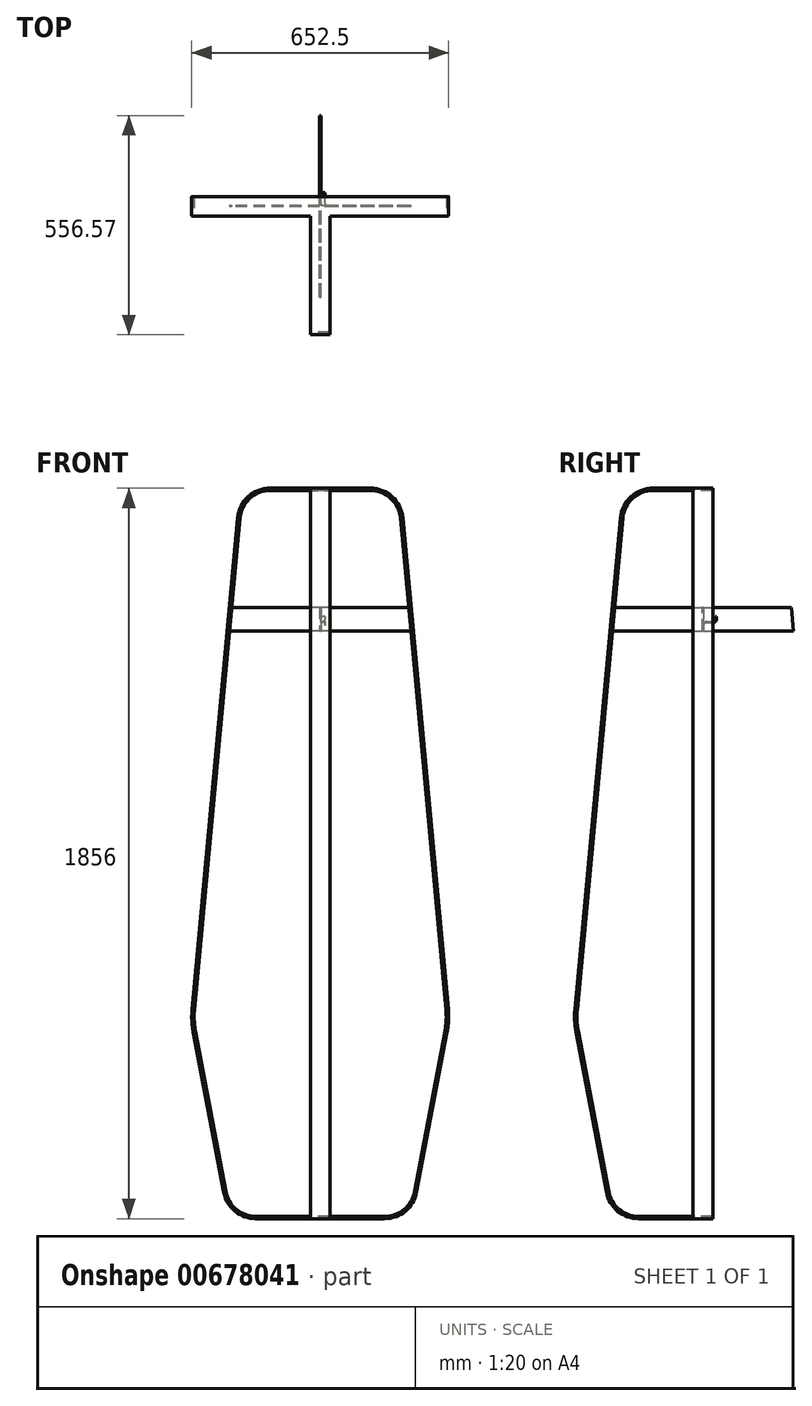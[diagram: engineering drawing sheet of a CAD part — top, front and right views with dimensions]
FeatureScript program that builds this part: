
annotation { "Feature Type Name" : "Feature", "Feature Type Description" : "" }
export const myFeature = defineFeature(function(context is Context, id is Id, definition is map)
    precondition{}
    {
        {
            var Q0;
            Q0=qCreatedBy(makeId("Front.planeOp"),FACE);
            var sketch = newSketch(context, id + "F0", { "sketchPlane" : qUnion([Q0])});
            skLineSegment(sketch, "E0", {"start": v(0, 0) * mm, "end": v(163.77, 0) * mm, "construction": true});
            skLineSegment(sketch, "E1", {"start": v(242.36, 65.07) * mm, "end": v(325, 500) * mm, "construction": true});
            skLineSegment(sketch, "E2", {"start": v(325, 500) * mm, "end": v(206.72, 1777.38) * mm, "construction": true});
            skLineSegment(sketch, "E3", {"start": v(127.07, 1850) * mm, "end": v(0, 1850) * mm, "construction": true});
            skLineSegment(sketch, "E4", {"start": v(0, 1850) * mm, "end": v(0, 0) * mm, "construction": true});
            skLineSegment(sketch, "E5", {"start": v(325, 500) * mm, "end": v(0, 500) * mm, "construction": true});
            skPoint(sketch, "E6.visualSharp", {"position": v(200, 1850) * mm});
            skArc(sketch, "E6.filletArc", {"start": v(206.72, 1777.38) * mm, "mid": v(180.96, 1829.12) * mm, "end": v(127.07, 1850) * mm, "construction": true});
            skPoint(sketch, "E7.visualSharp", {"position": v(230, 0) * mm});
            skArc(sketch, "E7.filletArc", {"start": v(163.77, 0) * mm, "mid": v(214.79, 18.38) * mm, "end": v(242.36, 65.07) * mm, "construction": true});
            skArc(sketch, "E8", {"start": v(319.74, 472.3) * mm, "mid": v(323.02, 500.1) * mm, "end": v(322.4, 528.07) * mm, "construction": true});
            skLineSegment(sketch, "E9", {"start": v(227.78, 1550) * mm, "end": v(0, 1550) * mm, "construction": true});
            skSolve(sketch);
        }
        {
            var Q0;
            Q0=qCreatedBy(makeId("Front.planeOp"),FACE);
            var sketch = newSketch(context, id + "F1", { "sketchPlane" : qUnion([Q0])});
            skLineSegment(sketch, "E10", {"start": v(0, 0) * mm, "end": v(163.77, 0) * mm});
            skArc(sketch, "E11", {"start": v(163.77, 0) * mm, "mid": v(214.79, 18.38) * mm, "end": v(242.36, 65.07) * mm});
            skLineSegment(sketch, "E12", {"start": v(322.4, 528.07) * mm, "end": v(206.72, 1777.38) * mm});
            skArc(sketch, "E13", {"start": v(206.72, 1777.38) * mm, "mid": v(180.96, 1829.12) * mm, "end": v(127.07, 1850) * mm});
            skLineSegment(sketch, "E14", {"start": v(127.07, 1850) * mm, "end": v(0, 1850) * mm});
            skLineSegment(sketch, "E15", {"start": v(242.36, 65.07) * mm, "end": v(319.74, 472.3) * mm});
            skArc(sketch, "E16", {"start": v(319.74, 472.3) * mm, "mid": v(323.02, 500.1) * mm, "end": v(322.4, 528.07) * mm});
            skSolve(sketch);
        }
        {
            var Q0;
            Q0=qCreatedBy(makeId("Right.planeOp"),FACE);
            var sketch = newSketch(context, id + "F2", { "sketchPlane" : qUnion([Q0])});
            skLineSegment(sketch, "E17.bottom", {"start": v(25, 3) * mm, "end": v(-25, 3) * mm});
            skLineSegment(sketch, "E17.top", {"start": v(25, -3) * mm, "end": v(-25, -3) * mm});
            skLineSegment(sketch, "E17.left", {"start": v(25, 3) * mm, "end": v(25, -3) * mm});
            skLineSegment(sketch, "E17.right", {"start": v(-25, 3) * mm, "end": v(-25, -3) * mm});
            skPoint(sketch, "E17.middle", {"position": v(0, 0) * mm});
            skSolve(sketch);
        }
        {
            var Q0;
            Q0 = qSketchRegion(id + "F2", true);
            var Q1;
            Q1=sQuery(id+"F1.wireOp",EDGE,"E10");
            var Q2;
            Q2=sQuery(id+"F1.wireOp",EDGE,"E11");
            var Q3;
            Q3=sQuery(id+"F1.wireOp",EDGE,"E15");
            var Q4;
            Q4=sQuery(id+"F1.wireOp",EDGE,"E16");
            var Q5;
            Q5=sQuery(id+"F1.wireOp",EDGE,"E12");
            var Q6;
            Q6=sQuery(id+"F1.wireOp",EDGE,"E13");
            var Q7;
            Q7=sQuery(id+"F1.wireOp",EDGE,"E14");
            sweep(context, id + "F3", {"profiles" : qUnion([Q0]), "path" : qUnion([Q1, Q2, Q3, Q4, Q5, Q6, Q7])});
        }
        {
            var Q0;
            Q0=qCreatedBy(makeId("Right.planeOp"),FACE);
            var sketch = newSketch(context, id + "F4", { "sketchPlane" : qUnion([Q0])});
            skLineSegment(sketch, "E18.bottom", {"start": v(1.5, 1550) * mm, "end": v(-1.5, 1550) * mm});
            skLineSegment(sketch, "E18.top", {"start": v(1.5, 1490) * mm, "end": v(-1.5, 1490) * mm});
            skLineSegment(sketch, "E18.left", {"start": v(1.5, 1550) * mm, "end": v(1.5, 1490) * mm});
            skLineSegment(sketch, "E18.right", {"start": v(-1.5, 1550) * mm, "end": v(-1.5, 1490) * mm});
            skPoint(sketch, "E18.middle", {"position": v(0, 1520) * mm});
            skSolve(sketch);
        }
        {
            var Q0;
            Q0=qCreatedBy(makeId("Right.planeOp"),FACE);
            var sketch = newSketch(context, id + "F5", { "sketchPlane" : qUnion([Q0])});
            skLineSegment(sketch, "E19.bottom", {"start": v(1.5, 1504) * mm, "end": v(-1.5, 1504) * mm, "construction": true});
            skLineSegment(sketch, "E19.top", {"start": v(1.5, 1490) * mm, "end": v(-1.5, 1490) * mm});
            skLineSegment(sketch, "E19.left", {"start": v(1.5, 1504) * mm, "end": v(1.5, 1490) * mm});
            skLineSegment(sketch, "E19.right", {"start": v(-1.5, 1504) * mm, "end": v(-1.5, 1490) * mm});
            skPoint(sketch, "E19.middle", {"position": v(0, 1497) * mm});
            skArc(sketch, "E20", {"start": v(8.5, 1514) * mm, "mid": v(1.43, 1511.07) * mm, "end": v(-1.5, 1504) * mm});
            skArc(sketch, "E21", {"start": v(8.5, 1511) * mm, "mid": v(3.55, 1508.95) * mm, "end": v(1.5, 1504) * mm});
            skLineSegment(sketch, "E22", {"start": v(8.5, 1511) * mm, "end": v(24.5, 1511) * mm});
            skLineSegment(sketch, "E23", {"start": v(8.5, 1514) * mm, "end": v(24.5, 1514) * mm});
            skArc(sketch, "E24", {"start": v(24.5, 1514) * mm, "mid": v(29.45, 1516.05) * mm, "end": v(31.5, 1521) * mm});
            skArc(sketch, "E25", {"start": v(24.5, 1511) * mm, "mid": v(31.57, 1513.93) * mm, "end": v(34.5, 1521) * mm});
            skLineSegment(sketch, "E26", {"start": v(31.5, 1521) * mm, "end": v(31.5, 1527) * mm});
            skLineSegment(sketch, "E27", {"start": v(31.5, 1527) * mm, "end": v(34.5, 1527) * mm});
            skLineSegment(sketch, "E28", {"start": v(34.5, 1527) * mm, "end": v(34.5, 1521) * mm});
            skSolve(sketch);
        }
        {
            var Q0;
            Q0 = qSketchRegion(id + "F5", true);
            extrude(context, id + "F6", {"entities" : qUnion([Q0]), "depth" : 12 * mm, "offsetDistance" : 25 * mm});
        }
        {
            var Q0;
            Q0=makeQuery(id+"F3.opSweep","SWEPT_BODY",BODY,{"disambiguationData":[OSD([sQuery(id+"F1.wireOp",EDGE,"E14"),sQuery(id+"F2.wireOp",EDGE,"E17.bottom"),sQuery(id+"F2.wireOp",EDGE,"E17.top"),sQuery(id+"F2.wireOp",EDGE,"E17.left"),sQuery(id+"F2.wireOp",EDGE,"E17.right")])]});
            var Q1;
            Q1=qCreatedBy(makeId("Right.planeOp"),FACE);
            mirror(context, id + "F7", {"operationType" : NewBodyOperationType.ADD, "entities" : qUnion([Q0]), "mirrorPlane" : qUnion([Q1])});
        }
        {
            var Q0;
            Q0 = qSketchRegion(id + "F4", true);
            extrude(context, id + "F8", {"entities" : qUnion([Q0]), "endBound" : BoundingType.UP_TO_NEXT, "depth" : 25 * mm, "offsetDistance" : 25 * mm, "hasSecondDirection" : true, "secondDirectionBound" : SecondDirectionBoundingType.UP_TO_NEXT, "secondDirectionOppositeDirection" : true, "secondDirectionDepth" : 25 * mm});
        }
        {
            var Q0;
            Q0=makeQuery(id+"F3.opSweep","SWEPT_BODY",BODY,{"disambiguationData":[OSD([sQuery(id+"F1.wireOp",EDGE,"E14"),sQuery(id+"F2.wireOp",EDGE,"E17.bottom"),sQuery(id+"F2.wireOp",EDGE,"E17.top"),sQuery(id+"F2.wireOp",EDGE,"E17.left"),sQuery(id+"F2.wireOp",EDGE,"E17.right")])]});
            var Q1;
            Q1=makeQuery(id+"F8.opExtrude","SWEPT_BODY",BODY,{"disambiguationData":[OSD([sQuery(id+"F4.wireOp",EDGE,"E18.bottom"),sQuery(id+"F4.wireOp",EDGE,"E18.top"),sQuery(id+"F4.wireOp",EDGE,"E18.left"),sQuery(id+"F4.wireOp",EDGE,"E18.right")])]});
            var Q2;
            Q2=sQuery(id+"F0.wireOp",EDGE,"E4");
            circularPattern(context, id + "F9", {"operationType" : NewBodyOperationType.ADD, "entities" : qUnion([Q0, Q1]), "axis" : qUnion([Q2]), "angle" : 180 * degree, "instanceCount" : 3, "equalSpace" : true});
        }
    });
